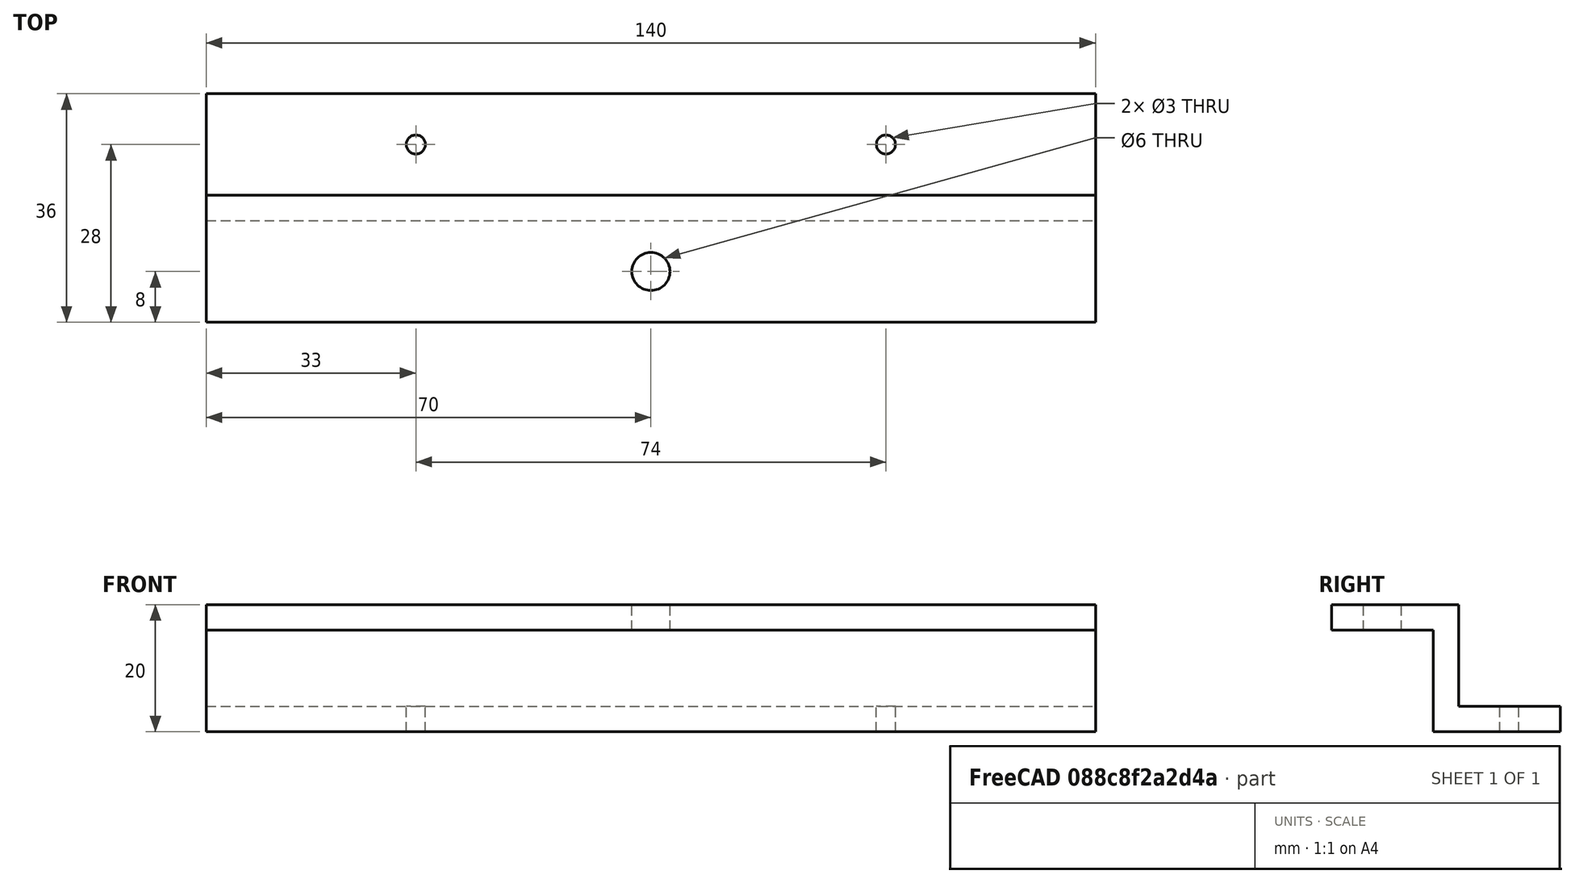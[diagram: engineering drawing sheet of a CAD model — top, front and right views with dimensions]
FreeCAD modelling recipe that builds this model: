
FCSTD DOCUMENT  (FreeCAD 0.15R4671 (Git))
Label: perfil z izquierdo
License: All rights reserved
LicenseURL: http://en.wikipedia.org/wiki/All_rights_reserved
objects: Part::Box×3, Part::Cylinder×3, Part::MultiFuse×2, Part::Cut×1, App::DocumentObjectGroup×1
note: 9 computed .brp shape members not serialized (recipe doc carries the construction recipe); baked Part::Feature solids carry a one-line shape summary decoded from their .brp

FEATURE [Part::Box] Box  label="perfil inferior"
  Height = 20
  Length = 140
  Width = 4
FEATURE [Part::Box] Box001  label="perfil intermedio"
  Height = 4
  Length = 140
  Width = 20
FEATURE [Part::Box] Box002  label="perfil superior"
  Height = 4
  Length = 140
  Placement = pos=(0,-16,16) rot=(0,0,1;0rad)
  Width = 20
FEATURE [Part::Cylinder] Cylinder  label="Agujero de metrica 3 delantero"
  Angle = 360
  Height = 4
  Placement = pos=(33,12,0) rot=(0,0,1;0rad)
  Radius = 1.5
FEATURE [Part::Cylinder] Cylinder001  label="Agujero de metrica 3 trasero"
  Angle = 360
  Height = 4
  Placement = pos=(107,12,0) rot=(0,0,1;0rad)
  Radius = 1.5
FEATURE [Part::Cylinder] Cylinder002  label="Agujero de metrica 6"
  Angle = 360
  Height = 4
  Placement = pos=(70,-8,16) rot=(0,0,1;0rad)
  Radius = 3
FEATURE [Part::MultiFuse] Fusion  label="Perfil z"
  Shapes = -> [Box,Box001,Box002]
FEATURE [Part::MultiFuse] Fusion001  label="Perforaciones"
  Shapes = -> [Cylinder002,Cylinder001,Cylinder]
FEATURE [Part::Cut] Cut  label="Perfil z izquierdo"
  Base = -> Fusion
  Tool = -> Fusion001
FEATURE [App::DocumentObjectGroup] Grupo  label="Perfil Z izquierdo"
  Group = -> [Cut]
